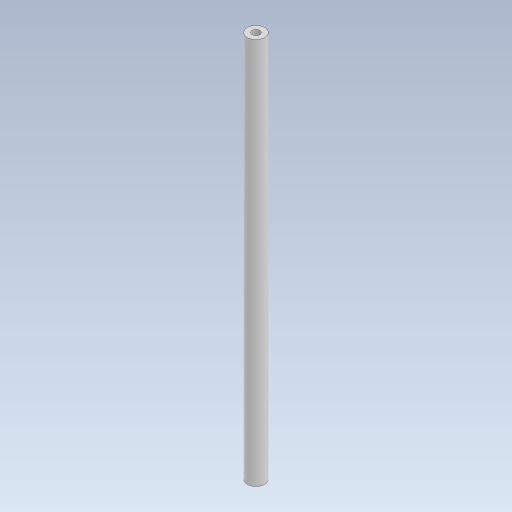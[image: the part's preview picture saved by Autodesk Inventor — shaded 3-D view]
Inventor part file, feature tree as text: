
AUTODESK INVENTOR PART (.ipt)
format: ipt  version: 2023.5 (Build 275446000, 446)  size: 234,496 bytes
history: native  units: mm
features: extrude x2, sketch x2
ambient origin geometry x8: Origin, YZ Plane, XZ Plane, XY Plane, X Axis, Y Axis, Z Axis, Center Point
bodies: Solid1 (feature_tree)
feature tree (4):
  extrude  "Extrusion1"  Depth=150.0mm TaperAngle=0.0deg
  extrude  "Extrusion2"  Depth=10.0mm TaperAngle=0.0deg
  sketch  "Sketch1"  dims[d0=6.8mm d1=150.0mm d2=0.0mm]
  sketch  "Sketch2"  dims[d3=3.0mm d4=10.0mm d5=0.0mm]
